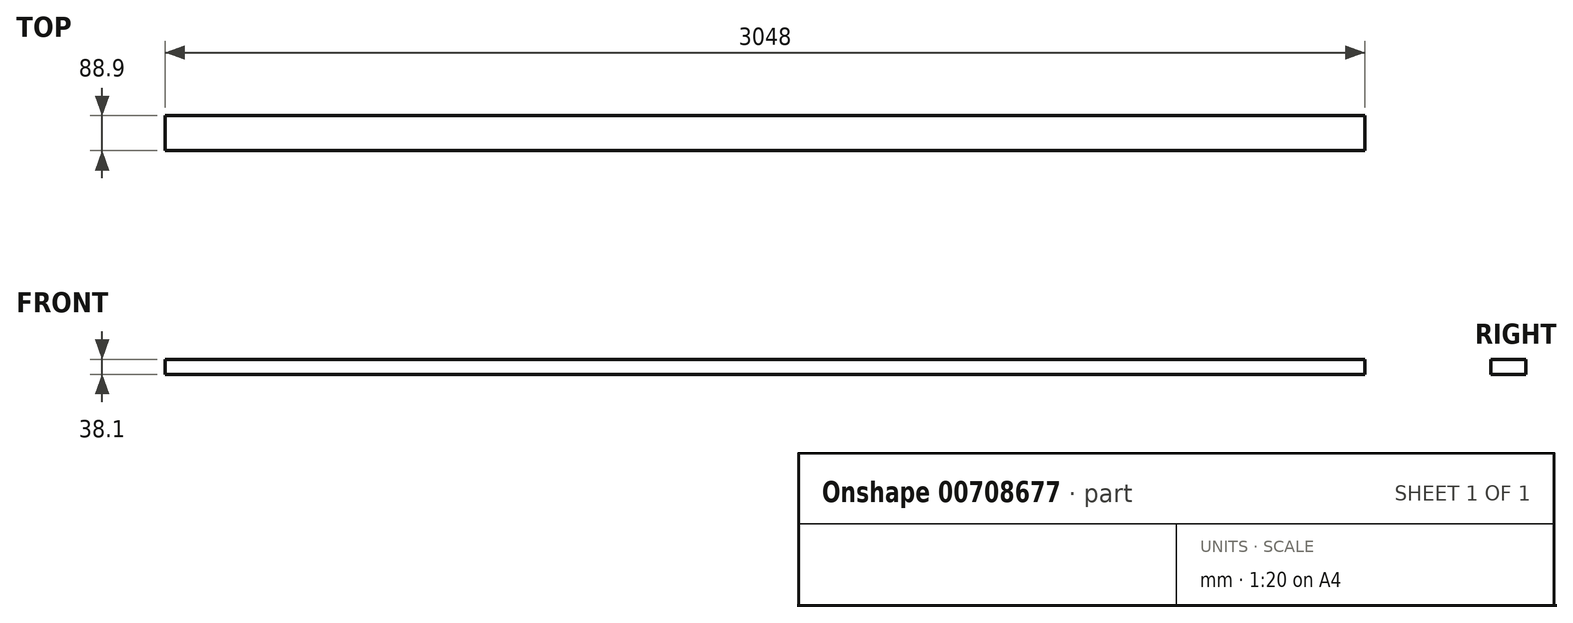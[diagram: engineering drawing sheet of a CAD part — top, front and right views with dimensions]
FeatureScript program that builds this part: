
annotation { "Feature Type Name" : "Feature", "Feature Type Description" : "" }
export const myFeature = defineFeature(function(context is Context, id is Id, definition is map)
    precondition{}
    {
        {
            var Q0;
            Q0=qCreatedBy(makeId("Right.planeOp"),FACE);
            var sketch = newSketch(context, id + "F0", { "sketchPlane" : qUnion([Q0])});
            skLineSegment(sketch, "E0.bottom", {"start": v(-92.67, 31.32) * mm, "end": v(-3.77, 31.32) * mm});
            skLineSegment(sketch, "E0.top", {"start": v(-92.67, -6.78) * mm, "end": v(-3.77, -6.78) * mm});
            skLineSegment(sketch, "E0.left", {"start": v(-92.67, 31.32) * mm, "end": v(-92.67, -6.78) * mm});
            skLineSegment(sketch, "E0.right", {"start": v(-3.77, 31.32) * mm, "end": v(-3.77, -6.78) * mm});
            skSolve(sketch);
        }
        {
            var Q0;
            Q0=makeQuery(id+"F0.imprint","IMPRINT",FACE,{"disambiguationData":[TD([[makeQuery(id+"F0.imprint","IMPRINT",EDGE,{"derivedFrom":sQuery(id+"F0.wireOp",EDGE,"E0.bottom")}),-1.0]])]});
            extrude(context, id + "F1", {"entities" : qUnion([Q0]), "endBound" : BoundingType.SYMMETRIC, "depth" : 3048 * mm, "offsetDistance" : 25.4 * mm});
        }
    });
